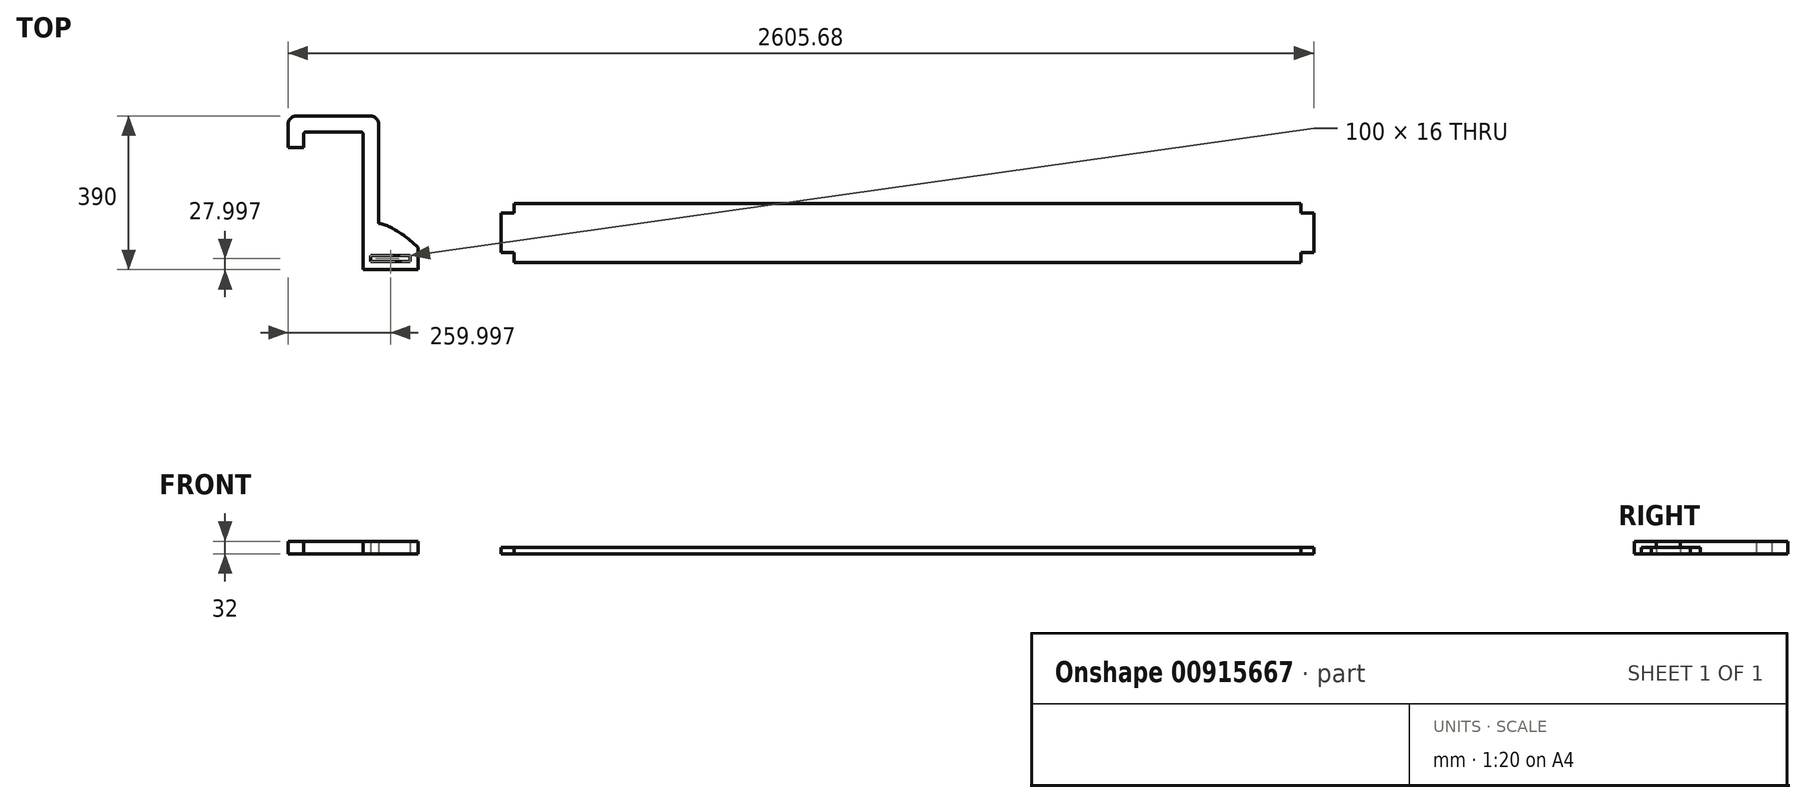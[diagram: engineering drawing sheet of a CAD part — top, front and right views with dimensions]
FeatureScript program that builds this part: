
annotation { "Feature Type Name" : "Feature", "Feature Type Description" : "" }
export const myFeature = defineFeature(function(context is Context, id is Id, definition is map)
    precondition{}
    {
        {
            var Q0;
            Q0=qCreatedBy(makeId("Top.planeOp"),FACE);
            var sketch = newSketch(context, id + "F0", { "sketchPlane" : qUnion([Q0])});
            skLineSegment(sketch, "E0.bottom", {"start": v(-302.66, 86.62) * mm, "end": v(1697.34, 86.62) * mm});
            skLineSegment(sketch, "E0.top", {"start": v(-302.66, -63.38) * mm, "end": v(1697.34, -63.38) * mm});
            skLineSegment(sketch, "E0.left", {"start": v(-302.66, 86.62) * mm, "end": v(-302.66, -63.38) * mm});
            skLineSegment(sketch, "E0.right", {"start": v(1697.34, 86.62) * mm, "end": v(1697.34, -63.38) * mm});
            skLineSegment(sketch, "E1.bottom", {"start": v(-666.34, -45.6) * mm, "end": v(-566.34, -45.6) * mm});
            skLineSegment(sketch, "E1.top", {"start": v(-666.34, -61.6) * mm, "end": v(-566.34, -61.6) * mm});
            skLineSegment(sketch, "E1.left", {"start": v(-666.34, -45.6) * mm, "end": v(-666.34, -61.6) * mm});
            skLineSegment(sketch, "E1.right", {"start": v(-566.34, -45.6) * mm, "end": v(-566.34, -61.6) * mm});
            skLineSegment(sketch, "E2.0", {"start": v(-686.34, -81.6) * mm, "end": v(-546.34, -81.6) * mm});
            skLineSegment(sketch, "E2.1", {"start": v(-686.34, -25.6) * mm, "end": v(-686.34, -81.6) * mm});
            skLineSegment(sketch, "E2.2", {"start": v(-686.34, -25.6) * mm, "end": v(-546.34, -25.6) * mm});
            skLineSegment(sketch, "E2.3", {"start": v(-546.34, -25.6) * mm, "end": v(-546.34, -81.6) * mm});
            skLineSegment(sketch, "E3", {"start": v(-686.34, -81.6) * mm, "end": v(-686.34, 263.4) * mm});
            skFitSpline(sketch, "E4", {"points": [v(-546.34, -25.6) * mm, v(-603.2, 18.7) * mm, v(-646.34, 36) * mm], "startDerivative": vector(-123.78, 117.46) * mm, "endDerivative": vector(-92.44, 10.38) * mm});
            skLineSegment(sketch, "E5", {"start": v(-646.34, 36) * mm, "end": v(-646.34, 288.4) * mm});
            skLineSegment(sketch, "E6", {"start": v(-666.34, 308.4) * mm, "end": v(-856.34, 308.4) * mm});
            skLineSegment(sketch, "E7", {"start": v(-876.34, 288.4) * mm, "end": v(-876.34, 268.4) * mm});
            skLineSegment(sketch, "E8", {"start": v(-876.34, 268.4) * mm, "end": v(-876.34, 228.4) * mm});
            skLineSegment(sketch, "E9", {"start": v(-876.34, 228.4) * mm, "end": v(-836.34, 228.4) * mm});
            skLineSegment(sketch, "E10", {"start": v(-836.34, 228.4) * mm, "end": v(-836.34, 263.4) * mm});
            skLineSegment(sketch, "E11", {"start": v(-831.34, 268.4) * mm, "end": v(-691.34, 268.4) * mm});
            skPoint(sketch, "E12.visualSharp", {"position": v(-646.34, 308.4) * mm});
            skArc(sketch, "E12.filletArc", {"start": v(-646.34, 288.4) * mm, "mid": v(-652.2, 302.55) * mm, "end": v(-666.34, 308.4) * mm});
            skPoint(sketch, "E13.visualSharp", {"position": v(-876.34, 308.4) * mm});
            skArc(sketch, "E13.filletArc", {"start": v(-856.34, 308.4) * mm, "mid": v(-870.48, 302.55) * mm, "end": v(-876.34, 288.4) * mm});
            skPoint(sketch, "E14.visualSharp", {"position": v(-836.34, 268.4) * mm});
            skArc(sketch, "E14.filletArc", {"start": v(-831.34, 268.4) * mm, "mid": v(-834.88, 266.94) * mm, "end": v(-836.34, 263.4) * mm});
            skPoint(sketch, "E15.visualSharp", {"position": v(-686.34, 268.4) * mm});
            skArc(sketch, "E15.filletArc", {"start": v(-686.34, 263.4) * mm, "mid": v(-687.8, 266.94) * mm, "end": v(-691.34, 268.4) * mm});
            skLineSegment(sketch, "E16.bottom", {"start": v(-334.66, 61.62) * mm, "end": v(-270.66, 61.62) * mm});
            skLineSegment(sketch, "E16.top", {"start": v(-334.66, -38.38) * mm, "end": v(-270.66, -38.38) * mm});
            skLineSegment(sketch, "E16.left", {"start": v(-334.66, 61.62) * mm, "end": v(-334.66, -38.38) * mm});
            skLineSegment(sketch, "E16.right", {"start": v(-270.66, 61.62) * mm, "end": v(-270.66, -38.38) * mm});
            skPoint(sketch, "E16.middle", {"position": v(-302.66, 11.62) * mm});
            skLineSegment(sketch, "E17", {"start": v(697.34, -63.38) * mm, "end": v(697.34, 86.62) * mm, "construction": true});
            skPoint(sketch, "E18.MirrorP", {"position": v(1697.34, 11.62) * mm});
            skLineSegment(sketch, "E19.MirrorCS", {"start": v(1729.34, 61.62) * mm, "end": v(1729.34, -38.38) * mm});
            skLineSegment(sketch, "E20.MirrorCS", {"start": v(1729.34, -38.38) * mm, "end": v(1665.34, -38.38) * mm});
            skLineSegment(sketch, "E21.MirrorCS", {"start": v(1665.34, 61.62) * mm, "end": v(1665.34, -38.38) * mm});
            skLineSegment(sketch, "E22.MirrorCS", {"start": v(1729.34, 61.62) * mm, "end": v(1665.34, 61.62) * mm});
            skLineSegment(sketch, "E23.bottom", {"start": v(-1196.7, -53.72) * mm, "end": v(-1296.7, -53.72) * mm});
            skLineSegment(sketch, "E23.top", {"start": v(-1196.7, -37.72) * mm, "end": v(-1296.7, -37.72) * mm});
            skLineSegment(sketch, "E23.left", {"start": v(-1196.7, -53.72) * mm, "end": v(-1196.7, -37.72) * mm});
            skLineSegment(sketch, "E23.right", {"start": v(-1296.7, -53.72) * mm, "end": v(-1296.7, -37.72) * mm});
            skPoint(sketch, "E23.middle", {"position": v(-1246.7, -45.72) * mm});
            skLineSegment(sketch, "E24", {"start": v(-1321.7, -68.72) * mm, "end": v(-1171.7, -68.72) * mm});
            skLineSegment(sketch, "E25", {"start": v(-1246.7, -37.72) * mm, "end": v(-1246.7, -77.48) * mm, "construction": true});
            skPoint(sketch, "E26", {"position": v(-1246.7, -68.72) * mm});
            skLineSegment(sketch, "E27", {"start": v(-1321.7, -68.72) * mm, "end": v(-1321.7, -27.15) * mm});
            skLineSegment(sketch, "E28", {"start": v(-1321.7, -27.15) * mm, "end": v(-1171.7, -27.15) * mm});
            skLineSegment(sketch, "E29", {"start": v(-1171.7, -27.15) * mm, "end": v(-1171.7, -68.72) * mm});
            skSolve(sketch);
        }
        {
            var Q0;
            {var subQ0=sQuery(id+"F0.wireOp",EDGE,"E2.2");Q0=makeQuery(id+"F0.imprint","IMPRINT",FACE,{"disambiguationData":[TD([[makeQuery(id+"F0.imprint","IMPRINT",EDGE,{"derivedFrom":subQ0}),1.0]])]});}
            var Q1;
            Q1=makeQuery(id+"F0.imprint","IMPRINT",FACE,{"disambiguationData":[TD([[makeQuery(id+"F0.imprint","IMPRINT",EDGE,{"derivedFrom":sQuery(id+"F0.wireOp",EDGE,"E1.bottom")}),1.0]])]});
            extrude(context, id + "F1", {"entities" : qUnion([Q0, Q1]), "depth" : 32 * mm, "offsetDistance" : 25 * mm});
        }
        {
            var Q0;
            {var subQ10=sQuery(id+"F0.wireOp",EDGE,"E0.bottom");Q0=makeQuery(id+"F0.imprint","IMPRINT",FACE,{"disambiguationData":[TD([[makeQuery(id+"F0.imprint","IMPRINT",EDGE,{"derivedFrom":subQ10}),-1.0]])]});}
            var Q1;
            {var subQ5=sQuery(id+"F0.wireOp",EDGE,"E21.MirrorCS");Q1=makeQuery(id+"F0.imprint","IMPRINT",FACE,{"disambiguationData":[TD([[makeQuery(id+"F0.imprint","IMPRINT",EDGE,{"derivedFrom":subQ5}),1.0]])]});}
            var Q2;
            {var subQ5=sQuery(id+"F0.wireOp",EDGE,"E16.left");Q2=makeQuery(id+"F0.imprint","IMPRINT",FACE,{"disambiguationData":[TD([[makeQuery(id+"F0.imprint","IMPRINT",EDGE,{"derivedFrom":subQ5}),1.0]])]});}
            var Q3;
            {var subQ5=sQuery(id+"F0.wireOp",EDGE,"E19.MirrorCS");Q3=makeQuery(id+"F0.imprint","IMPRINT",FACE,{"disambiguationData":[TD([[makeQuery(id+"F0.imprint","IMPRINT",EDGE,{"derivedFrom":subQ5}),-1.0]])]});}
            var Q4;
            {var subQ5=sQuery(id+"F0.wireOp",EDGE,"E16.right");Q4=makeQuery(id+"F0.imprint","IMPRINT",FACE,{"disambiguationData":[TD([[makeQuery(id+"F0.imprint","IMPRINT",EDGE,{"derivedFrom":subQ5}),-1.0]])]});}
            extrude(context, id + "F2", {"entities" : qUnion([Q0, Q1, Q2, Q3, Q4]), "depth" : 16 * mm, "offsetDistance" : 25 * mm});
        }
    });
